# Revit family: Interceptor_Grease-Zurn-GT2702
name_source: partatom
category: Plumbing Fixtures
units: mm (PartAtom-declared; Revit-internal decimal feet)

## family parameters
Always vertical = Yes
Cut with Voids When Loaded = No
Maintain Annotation Orientation = No
OmniClass Number = 23.45.30.00
OmniClass Title = Washing and Waste Disposal Equipment
Part Type = Normal
Room Calculation Point = No
Round Connector Dimension = Use Radius
Shared = No
Work Plane-Based = No

## types (9) — shared parameters
Assembly Code = D2090300
Body Offset 02 = 2.25 "
CW Connection = No
Cover Diameter = 1.5 "
Cover Diameter_2 = 1.539 "
Default Elevation = 20 "
Description = Polyethylene Grease Interceptor
HW Connection = No
Manufacturer = Zurn Water, LLC
Manufacturer Brand = Zurn
Material = Steel - Zurn - Stainless - Type - 304
Model = GT2702
Modified Date = 01/09/2026
Product Documentation Link = https://files.zurn.com
Product Installation Sheet URL = https://files.zurn.com
Product Page URL = https://www.zurn.com
Product data URL = https://bimobject.com
URL = www.zurn.com
Vent Connection = No
WFU = 1
Waste Connection = Yes
zero-valued in all types: CWFU, HWFU

## per-type parameters (varying)
| type | Body Offset 01 | Body Offset 03 | C Dimension | D Dimension | E Dimension | F Dimension | Flow Rate G.P.M. | G Dimension | Grease Capacity Lbs. | Liquid Holding Capacity Gal. (L) | Pipe Size_A Inside Radius | Pipe Size_A Nominal Radius | Pipe Size_A Outer Radius | Type Comments |
| GT2702-75-3 NPT | 2.25 " | 2 " | 25 " | 5.75 " | 5.75 " | 44.25 " | 75 " | 25 " | 150 " | 61.8 " | 1.534 " | 1.5 " | 1.75 " | GT2702-75 3 Inch Female NPT |
| GT2702-50-3 NPT | 2 " | 2 " | 18 " | 4 " | 4 " | 37 " | 50 " | 25 " | 100 " | 35.5 " | 1.534 " | 1.5 " | 1.75 " | GT2702-50 3 Inch Female NPT |
| GT2702-35-3 NPT | 2.25 " | 2 " | 18 " | 4 " | 4 " | 32.5 " | 35 " | 22 " | 70 " | 26.1 " | 1.534 " | 1.5 " | 1.75 " | GT2702-35 3 Inch Female NPT |
| GT2702-25-3 NPT | 2.25 " | 2 " | 17 " | 4 " | 4 " | 32.5 " | 25 " | 19.5 " | 50 " | 20.8 " | 1.534 " | 1.5 " | 1.75 " | GT2702-25 3 Inch Female NPT |
| GT2702-20-2 NPT | 2.25 " | 2 " | 14 " | 3.5 " | 3.5 " | 29 " | 20 " | 19.5 " | 40 " | 15 " | 1.034 " | 1 " | 1.188 " | GT2702-20 2 Inch Female NPT |
| GT2702-15-2 NPT | 2.25 " | 2 " | 13 " | 3.5 " | 3.5 " | 23 " | 15 " | 19.5 " | 30 " | 10.2 " | 1.034 " | 1 " | 1.188 " | GT2702-15 2 Inch Female NPT |
| GT2702-10-2 NPT | 2.25 " | 2 " | 12 " | 3.5 " | 3.5 " | 23 " | 10 " | 14.5 " | 20 " | 6 " | 1.034 " | 1 " | 1.188 " | GT2702-10 2 Inch Female NPT |
| GT2702-07-2 NPT | 2.25 " | 2 " | 11 " | 3.25 " | 3.25 " | 20 " | 7 " | 14.5 " | 14 " | 4.6 " | 1.034 " | 1 " | 1.188 " | GT2702-07 2 Inch Female NPT |
| GT2702-04-2 NPT | 2 " | 1.75 " | 9.5 " | 2 " | 2 " | 15 " | 4 " | 10 " | 8 " | 1.5 " | 1.034 " | 1 " | 1.188 " | GT2702-04 2 Inch Female NPT |

## geometry (parser evidence)
native form markers: Sweep x3
no freeform markers — native parametric forms only
